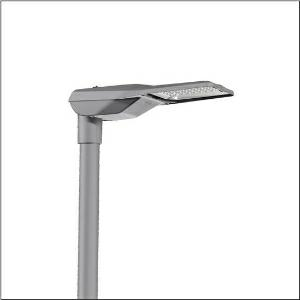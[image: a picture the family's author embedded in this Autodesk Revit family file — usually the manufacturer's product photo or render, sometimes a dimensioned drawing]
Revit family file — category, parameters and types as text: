
# Revit family: streetlight_sl_21_mini___st0_5a_5xe2b33s08jb_541c
name_source: partatom
category: Lighting Fixtures
units: mm (PartAtom-declared; Revit-internal decimal feet)

## family parameters
Cut with Voids When Loaded = No
Host = Face
Light Source = No
Part Type = Normal
Room Calculation Point = No
Round Connector Dimension = Use Diameter
Shared = No

## types (1)
- --- (1 x LED, 12940 lm, 88.6 W, 3000K)
    Apparent Load = 89 VA
    CIE Flux Codes = 43 76 97 100 100
    Color Rendering = 70
    Color Temperature = 3000K
    Default Elevation = 1800 mm
    Description = Streetlight SL 21 mini, mast luminaire, primary light control with lens, of PMMA, primary optical cover: cover, of toughened safety glass, transparent, light distribution: ST0.5a, light emission: direct distribution, primary light characteristic: asymmetric, installation type: side-entry, post-top, LED, High Power LED, rated luminous flux: 12.940lm, luminous efficacy: 146lm/W, light colour: 730, colour temperature: 3000K, control gear: D4i, control: overheat protection, constant luminous flux control, time-dependent luminous flux control, flexible luminous flux parameterisation, pre-setting: logarithmic dimming characteristic, mains connection: 220..240V, AC, 50/60Hz, start of lifetime: 89W, end of service life: 92W, reduction: 41W, luminaire housing, of diecast aluminium, powder-coated, SITECO metallic grey (DB 702S), corrosivity category C5 high according to DIN EN ISO 12944, please order mast flange separately, inclination adjustable: 0°, 5°, 10°, 15°, sealing non-destructively replaceable, multi-level sealing system, length: 628mm, width: 235mm, height: 110mm, mast flange for spigot size: 42mm (side-entry): 5XC10008XM4, 60/48mm (side-entry/post-top): 5XC10108XM2, 76/60mm (side-entry/post-top): 5XC10108XM1, mounting height: 4..8m, Smart Interface above, protection rating (complete): IP66, insulation class (complete): insulation class II (safety insulation), certification: CE, ENEC, ENEC+, VDE, impact resistance: IK10, permissible operating ambient temperature for outdoor applications: -40..+50°C, standard-compliant lighting for roads and squares, packaging unit: 1 piece

Light Distribution: ST0.5a
    Height = 110 mm
    Lamp = 1 x LED
    Lamp Light Flux = 12940 lm
    Lamp Power = 88.6 W
    Lamp count = 1
    Length = 625 mm
    Luminous efficacy = 146 lm/W
    Manufacturer = Siteco
    ModVariant = No
    Model = 5XE2B33S08JB
    Number of Poles = 1
    OnlyDefault = Yes
    Power Factor = 1
    Product Name = Streetlight SL 21 mini | ST0.5a
    Product group = mast luminaire | pylon top
    ProductGroupID = 6100
    Protection Class = Protection class II
    Protection Degree = IP 66
    RLX_Detail_Level = 1
    RLX_Emergency_Light_Flux = 0 lm
    RLX_Emergency_Type = 0
    RLX_Emergency_Type_DB = No
    RlxData = <blob elided: 37469 chars, md5=6a1f17f5>
    Socket = socket
    Standby Power = 0 W
    System Light Flux = 12940 lm
    System Power = 89 W
    Type Comments = factory setting: luminous flux: 100 % | dim-lin: 254 | 915 mA
    Type Image = l_1003515.jpg
    URL = http://relux.com
    VarID = @adj_031957
    Voltage = 0 V
    Weight = 0.00 kg
    Width = 234 mm

## geometry (parser evidence)
native form markers: Blend x4, Sweep x10
no freeform markers — native parametric forms only
